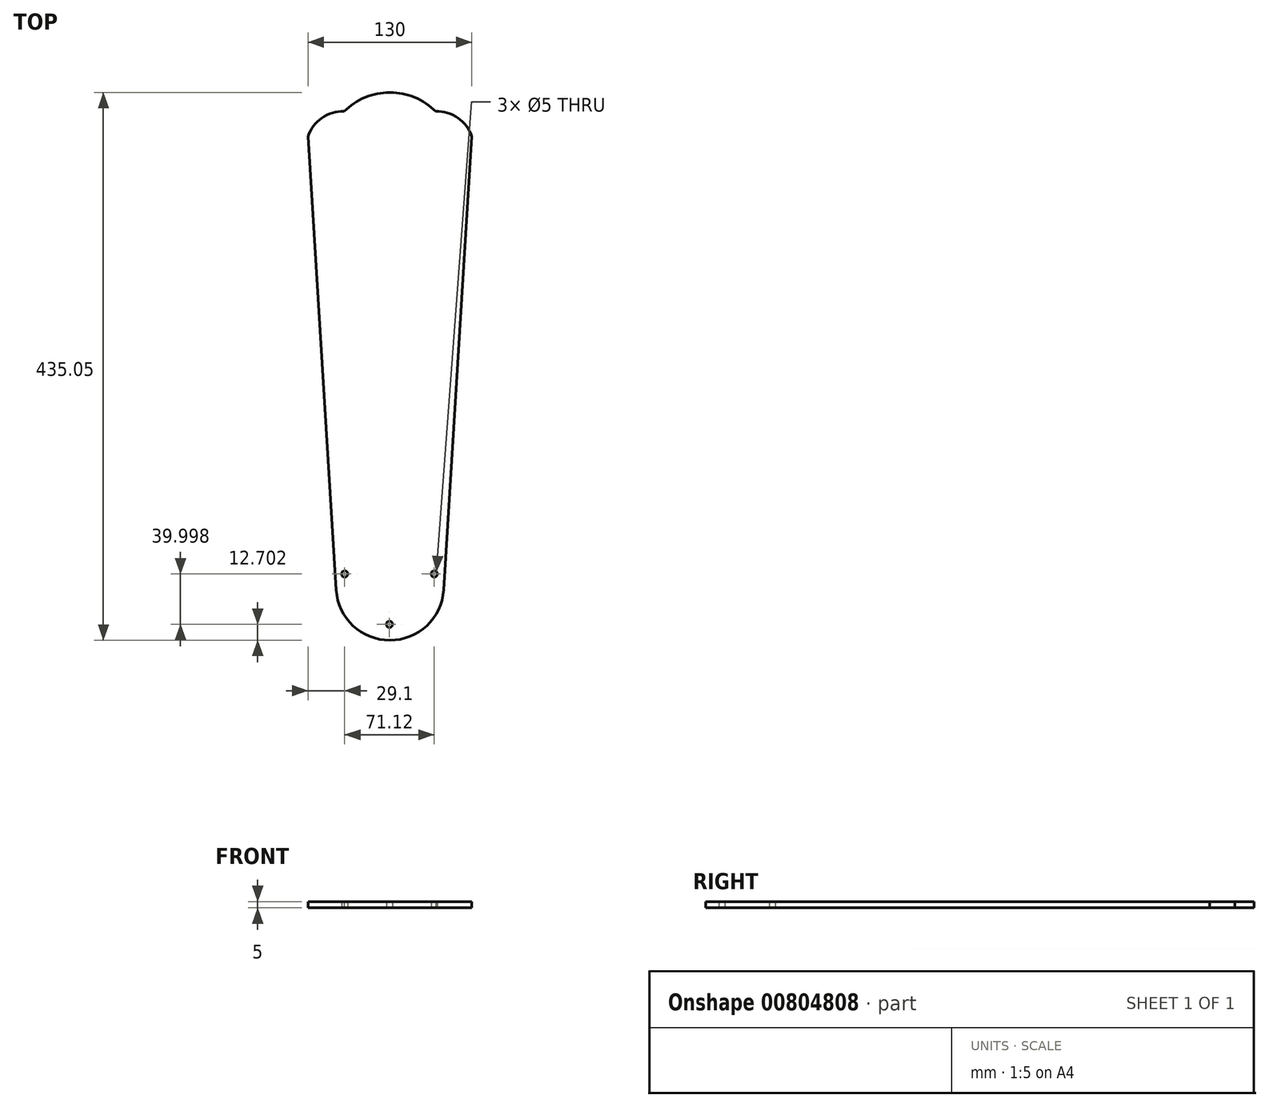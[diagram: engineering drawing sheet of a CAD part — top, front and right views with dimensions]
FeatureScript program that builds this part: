
annotation { "Feature Type Name" : "Feature", "Feature Type Description" : "" }
export const myFeature = defineFeature(function(context is Context, id is Id, definition is map)
    precondition{}
    {
        {
            var Q0;
            Q0=qCreatedBy(makeId("Top.planeOp"),FACE);
            var sketch = newSketch(context, id + "F0", { "sketchPlane" : qUnion([Q0])});
            skLineSegment(sketch, "E0", {"start": v(-42.29, -18.6) * mm, "end": v(42.97, -18.6) * mm});
            skArc(sketch, "E1", {"start": v(-42.29, -18.6) * mm, "mid": v(0.34, -58.6) * mm, "end": v(42.97, -18.6) * mm});
            skLineSegment(sketch, "E2", {"start": v(-64.66, 341.37) * mm, "end": v(65.34, 341.37) * mm});
            skPoint(sketch, "E3", {"position": v(0.34, 341.37) * mm});
            skPoint(sketch, "E4", {"position": v(0.34, -18.6) * mm});
            skLineSegment(sketch, "E5", {"start": v(-64.66, 341.37) * mm, "end": v(-42.29, -18.6) * mm});
            skLineSegment(sketch, "E6", {"start": v(65.34, 341.37) * mm, "end": v(42.97, -18.6) * mm});
            skArc(sketch, "E7", {"start": v(-36, 361.37) * mm, "mid": v(-53.67, 356.16) * mm, "end": v(-64.66, 341.37) * mm});
            skArc(sketch, "E8.MirrorCS", {"start": v(36.68, 361.37) * mm, "mid": v(54.35, 356.16) * mm, "end": v(65.34, 341.37) * mm});
            skArc(sketch, "E9", {"start": v(36.68, 361.37) * mm, "mid": v(0.34, 376.45) * mm, "end": v(-36, 361.37) * mm});
            skCircle(sketch, "E10", {"center": v(0, -45.9) * mm, "radius": 2.5 * mm});
            skCircle(sketch, "E11", {"center": v(-35.56, -5.9) * mm, "radius": 2.5 * mm});
            skCircle(sketch, "E12", {"center": v(35.56, -5.9) * mm, "radius": 2.5 * mm});
            skSolve(sketch);
        }
        {
            var Q0;
            Q0=qSketchRegion(id+"F0",true);
            extrude(context, id + "F1", {"entities" : qUnion([Q0]), "depth" : 5 * mm});
        }
    });
